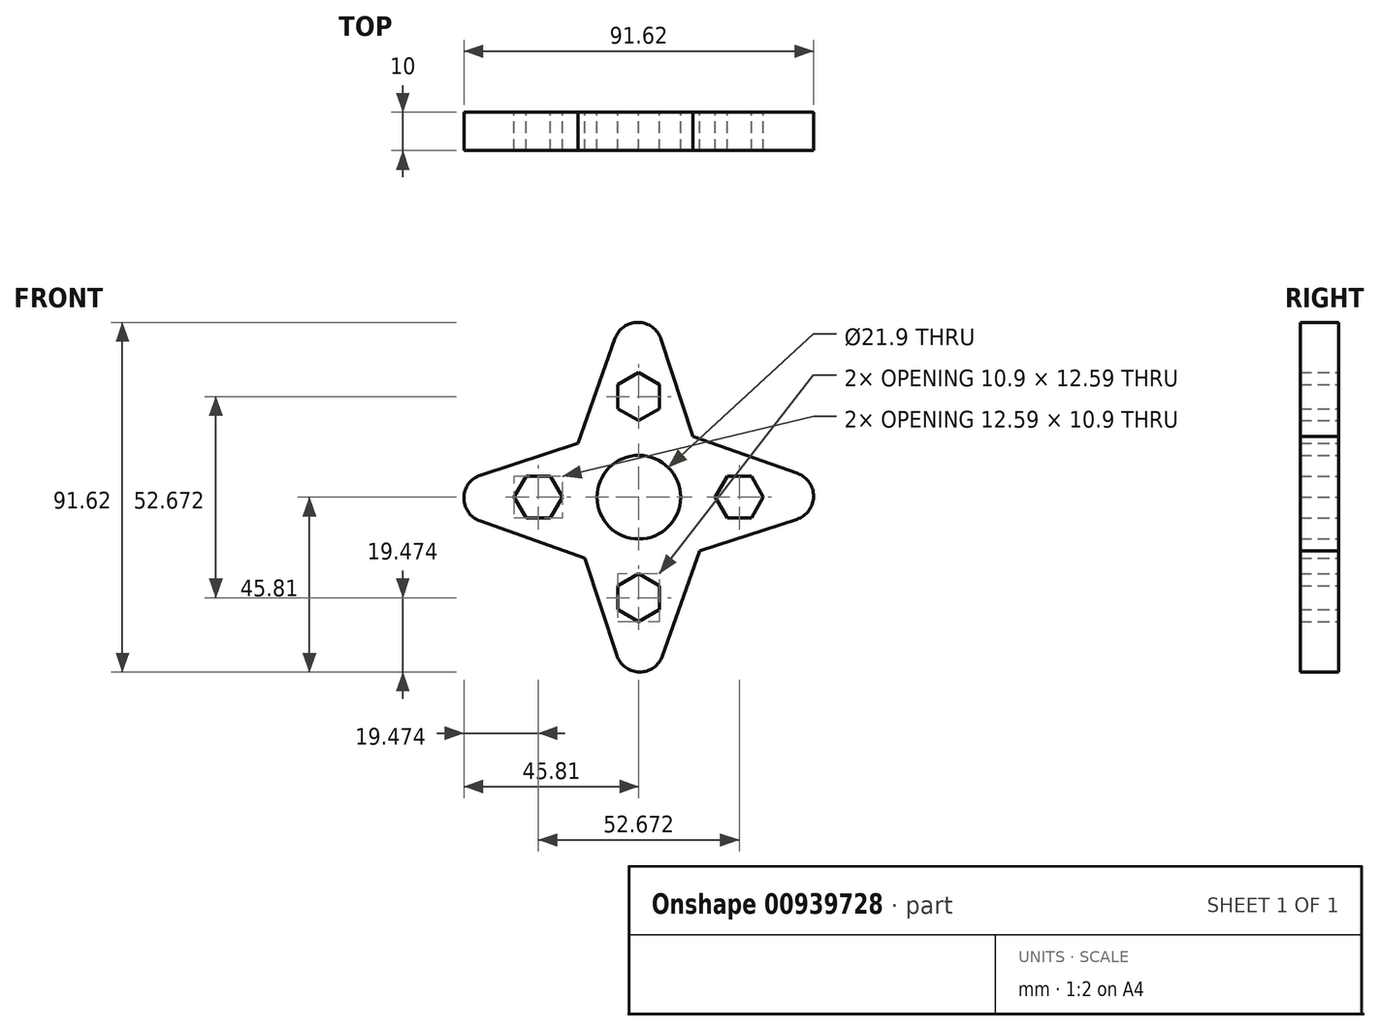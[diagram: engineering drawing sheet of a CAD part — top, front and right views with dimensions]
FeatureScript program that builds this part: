
annotation { "Feature Type Name" : "Feature", "Feature Type Description" : "" }
export const myFeature = defineFeature(function(context is Context, id is Id, definition is map)
    precondition{}
    {
        {
            var Q0;
            Q0=qCreatedBy(makeId("Front.planeOp"),FACE);
            var sketch = newSketch(context, id + "F0", { "sketchPlane" : qUnion([Q0])});
            skLineSegment(sketch, "E0", {"start": v(-15.95, 14.12) * mm, "end": v(-6.23, 41.57) * mm});
            skLineSegment(sketch, "E1", {"start": v(5.8, 41.43) * mm, "end": v(14.12, 15.95) * mm});
            skCircle(sketch, "E2", {"center": v(0, 0) * mm, "radius": 10.95 * mm});
            skCircle(sketch, "E3.cCircle", {"center": v(0, 26.34) * mm, "radius": 5.45 * mm, "construction": true});
            skLineSegment(sketch, "E3.0", {"start": v(5.45, 29.48) * mm, "end": v(0, 32.63) * mm});
            skLineSegment(sketch, "E3.1", {"start": v(5.45, 23.19) * mm, "end": v(5.45, 29.48) * mm});
            skLineSegment(sketch, "E3.2", {"start": v(0, 20.04) * mm, "end": v(5.45, 23.19) * mm});
            skLineSegment(sketch, "E3.3", {"start": v(-5.45, 23.19) * mm, "end": v(0, 20.04) * mm});
            skLineSegment(sketch, "E3.4", {"start": v(-5.45, 29.48) * mm, "end": v(-5.45, 23.19) * mm});
            skLineSegment(sketch, "E3.5", {"start": v(0, 32.63) * mm, "end": v(-5.45, 29.48) * mm});
            skPoint(sketch, "E3.0.midPoint", {"position": v(2.73, 31.06) * mm});
            skPoint(sketch, "E4", {"position": v(-5.45, 26.34) * mm});
            skCircle(sketch, "E5.1.0", {"center": v(-26.34, 0) * mm, "radius": 5.45 * mm, "construction": true});
            skPoint(sketch, "E5.1.1", {"position": v(-31.06, 2.72) * mm});
            skPoint(sketch, "E5.1.2", {"position": v(-26.34, -5.45) * mm});
            skLineSegment(sketch, "E5.1.3", {"start": v(-20.04, 0) * mm, "end": v(-23.19, 5.45) * mm});
            skLineSegment(sketch, "E5.1.4", {"start": v(-23.19, 5.45) * mm, "end": v(-29.48, 5.45) * mm});
            skLineSegment(sketch, "E5.1.5", {"start": v(-32.63, 0) * mm, "end": v(-29.48, -5.45) * mm});
            skLineSegment(sketch, "E5.1.6", {"start": v(-29.48, -5.45) * mm, "end": v(-23.19, -5.45) * mm});
            skLineSegment(sketch, "E5.1.7", {"start": v(-23.19, -5.45) * mm, "end": v(-20.04, 0) * mm});
            skLineSegment(sketch, "E5.1.8", {"start": v(-29.48, 5.45) * mm, "end": v(-32.63, 0) * mm});
            skLineSegment(sketch, "E5.1.9", {"start": v(-41.43, 5.8) * mm, "end": v(-15.95, 14.12) * mm});
            skLineSegment(sketch, "E5.1.10", {"start": v(-14.12, -15.95) * mm, "end": v(-41.57, -6.23) * mm});
            skCircle(sketch, "E5.2.0", {"center": v(0, -26.34) * mm, "radius": 5.45 * mm, "construction": true});
            skPoint(sketch, "E5.2.1", {"position": v(-2.73, -31.06) * mm});
            skPoint(sketch, "E5.2.2", {"position": v(5.45, -26.34) * mm});
            skLineSegment(sketch, "E5.2.3", {"start": v(0, -20.04) * mm, "end": v(-5.45, -23.19) * mm});
            skLineSegment(sketch, "E5.2.4", {"start": v(-5.45, -23.19) * mm, "end": v(-5.45, -29.48) * mm});
            skLineSegment(sketch, "E5.2.5", {"start": v(0, -32.63) * mm, "end": v(5.45, -29.48) * mm});
            skLineSegment(sketch, "E5.2.6", {"start": v(5.45, -29.48) * mm, "end": v(5.45, -23.19) * mm});
            skLineSegment(sketch, "E5.2.7", {"start": v(5.45, -23.19) * mm, "end": v(0, -20.04) * mm});
            skLineSegment(sketch, "E5.2.8", {"start": v(-5.45, -29.48) * mm, "end": v(0, -32.63) * mm});
            skLineSegment(sketch, "E5.2.9", {"start": v(-5.8, -41.43) * mm, "end": v(-14.12, -15.95) * mm});
            skLineSegment(sketch, "E5.2.10", {"start": v(15.95, -14.12) * mm, "end": v(6.23, -41.57) * mm});
            skCircle(sketch, "E5.3.0", {"center": v(26.34, 0) * mm, "radius": 5.45 * mm, "construction": true});
            skPoint(sketch, "E5.3.1", {"position": v(31.06, -2.72) * mm});
            skPoint(sketch, "E5.3.2", {"position": v(26.34, 5.45) * mm});
            skLineSegment(sketch, "E5.3.3", {"start": v(20.04, 0) * mm, "end": v(23.19, -5.45) * mm});
            skLineSegment(sketch, "E5.3.4", {"start": v(23.19, -5.45) * mm, "end": v(29.48, -5.45) * mm});
            skLineSegment(sketch, "E5.3.5", {"start": v(32.63, 0) * mm, "end": v(29.48, 5.45) * mm});
            skLineSegment(sketch, "E5.3.6", {"start": v(29.48, 5.45) * mm, "end": v(23.19, 5.45) * mm});
            skLineSegment(sketch, "E5.3.7", {"start": v(23.19, 5.45) * mm, "end": v(20.04, 0) * mm});
            skLineSegment(sketch, "E5.3.8", {"start": v(29.48, -5.45) * mm, "end": v(32.63, 0) * mm});
            skLineSegment(sketch, "E5.3.9", {"start": v(41.43, -5.8) * mm, "end": v(15.95, -14.12) * mm});
            skLineSegment(sketch, "E5.3.10", {"start": v(14.12, 15.95) * mm, "end": v(41.57, 6.23) * mm});
            skPoint(sketch, "E6.visualSharp", {"position": v(59.17, 0) * mm});
            skArc(sketch, "E6.filletArc", {"start": v(41.43, -5.8) * mm, "mid": v(45.8, 0.16) * mm, "end": v(41.57, 6.23) * mm});
            skPoint(sketch, "E7.visualSharp", {"position": v(0, 59.17) * mm});
            skArc(sketch, "E7.filletArc", {"start": v(5.8, 41.43) * mm, "mid": v(-0.16, 45.8) * mm, "end": v(-6.23, 41.57) * mm});
            skPoint(sketch, "E8.visualSharp", {"position": v(-59.17, 0) * mm});
            skArc(sketch, "E8.filletArc", {"start": v(-41.43, 5.8) * mm, "mid": v(-45.8, -0.16) * mm, "end": v(-41.57, -6.23) * mm});
            skPoint(sketch, "E9.visualSharp", {"position": v(0, -59.17) * mm});
            skArc(sketch, "E9.filletArc", {"start": v(-5.8, -41.43) * mm, "mid": v(0.16, -45.8) * mm, "end": v(6.23, -41.57) * mm});
            skSolve(sketch);
        }
        {
            var Q0;
            Q0=makeQuery(id+"F0.imprint","IMPRINT",FACE,{"disambiguationData":[TD([[makeQuery(id+"F0.imprint","IMPRINT",EDGE,{"derivedFrom":sQuery(id+"F0.wireOp",EDGE,"E0")}),-1.0]])]});
            extrude(context, id + "F1", {"entities" : qUnion([Q0]), "depth" : 10 * mm, "offsetDistance" : 25.4 * mm});
        }
    });
